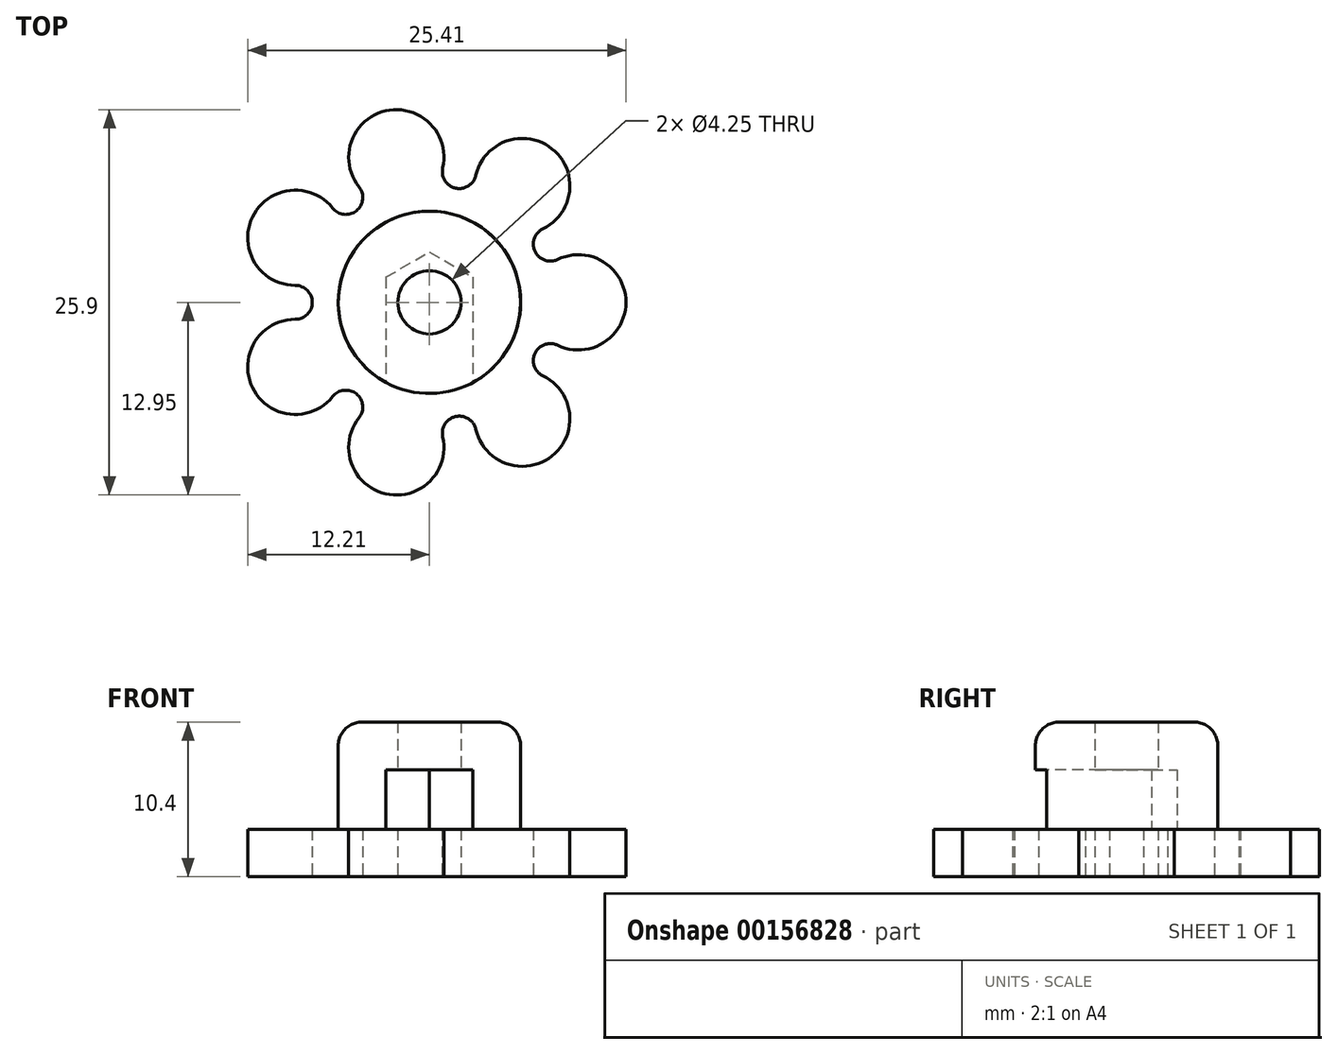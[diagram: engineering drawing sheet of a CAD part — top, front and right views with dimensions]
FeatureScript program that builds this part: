
annotation { "Feature Type Name" : "Feature", "Feature Type Description" : "" }
export const myFeature = defineFeature(function(context is Context, id is Id, definition is map)
    precondition{}
    {
        {
            var Q0;
            Q0=qCreatedBy(makeId("Top.planeOp"),FACE);
            var sketch = newSketch(context, id + "F0", { "sketchPlane" : qUnion([Q0])});
            skCircle(sketch, "E0", {"center": v(0, 0) * mm, "radius": 2.12 * mm});
            skArc(sketch, "E1", {"start": v(8.61, 2.88) * mm, "mid": v(13.2, 0) * mm, "end": v(8.61, -2.88) * mm});
            skArc(sketch, "E2.1.0", {"start": v(3.12, 8.53) * mm, "mid": v(8.23, 10.32) * mm, "end": v(7.62, 4.94) * mm});
            skArc(sketch, "E2.2.0", {"start": v(-4.73, 7.75) * mm, "mid": v(-2.94, 12.87) * mm, "end": v(0.9, 9.04) * mm});
            skArc(sketch, "E2.3.0", {"start": v(-9, 1.14) * mm, "mid": v(-11.9, 5.73) * mm, "end": v(-6.5, 6.33) * mm});
            skArc(sketch, "E2.4.0", {"start": v(-6.5, -6.33) * mm, "mid": v(-11.9, -5.73) * mm, "end": v(-9, -1.14) * mm});
            skArc(sketch, "E2.5.0", {"start": v(0.9, -9.04) * mm, "mid": v(-2.94, -12.87) * mm, "end": v(-4.73, -7.75) * mm});
            skArc(sketch, "E2.6.0", {"start": v(7.62, -4.94) * mm, "mid": v(8.23, -10.32) * mm, "end": v(3.12, -8.53) * mm});
            skLineSegment(sketch, "E3", {"start": v(7.62, -4.94) * mm, "end": v(8.61, -2.88) * mm, "construction": true});
            skArc(sketch, "E4", {"start": v(8.61, -2.88) * mm, "mid": v(7.1, -3.42) * mm, "end": v(7.62, -4.94) * mm});
            skArc(sketch, "E5.1.0", {"start": v(7.62, 4.94) * mm, "mid": v(7.1, 3.42) * mm, "end": v(8.61, 2.88) * mm});
            skArc(sketch, "E5.2.0", {"start": v(0.9, 9.04) * mm, "mid": v(1.75, 7.67) * mm, "end": v(3.12, 8.53) * mm});
            skArc(sketch, "E5.3.0", {"start": v(-6.5, 6.33) * mm, "mid": v(-4.9, 6.15) * mm, "end": v(-4.73, 7.75) * mm});
            skArc(sketch, "E5.4.0", {"start": v(-9, -1.14) * mm, "mid": v(-7.87, 0) * mm, "end": v(-9, 1.14) * mm});
            skArc(sketch, "E5.5.0", {"start": v(-4.73, -7.75) * mm, "mid": v(-4.9, -6.15) * mm, "end": v(-6.5, -6.33) * mm});
            skArc(sketch, "E5.6.0", {"start": v(3.12, -8.53) * mm, "mid": v(1.75, -7.67) * mm, "end": v(0.9, -9.04) * mm});
            skCircle(sketch, "E6.cCircle", {"center": v(0, 0) * mm, "radius": 2.93 * mm, "construction": true});
            skLineSegment(sketch, "E6.0", {"start": v(2.93, 1.69) * mm, "end": v(2.93, -1.69) * mm, "construction": true});
            skLineSegment(sketch, "E6.1", {"start": v(2.92, -1.69) * mm, "end": v(0, -3.38) * mm, "construction": true});
            skLineSegment(sketch, "E6.2", {"start": v(0, -3.38) * mm, "end": v(-2.92, -1.69) * mm, "construction": true});
            skLineSegment(sketch, "E6.3", {"start": v(-2.93, -1.69) * mm, "end": v(-2.93, 1.69) * mm, "construction": true});
            skLineSegment(sketch, "E6.4", {"start": v(-2.93, 1.69) * mm, "end": v(0, 3.38) * mm, "construction": true});
            skLineSegment(sketch, "E6.5", {"start": v(0, 3.38) * mm, "end": v(2.93, 1.69) * mm, "construction": true});
            skPoint(sketch, "E6.0.midPoint", {"position": v(2.93, 0) * mm});
            skSolve(sketch);
        }
        {
            var Q0;
            Q0=qSketchRegion(id+"F0",true);
            extrude(context, id + "F1", {"entities" : qUnion([Q0]), "depth" : 3.2 * mm});
        }
        {
            var Q0;
            Q0=makeQuery(id+"F1.opExtrude","CAP_FACE",FACE,{"disambiguationData":[OSD([sQuery(id+"F0.wireOp",EDGE,"E0"),sQuery(id+"F0.wireOp",EDGE,"E1"),sQuery(id+"F0.wireOp",EDGE,"E2.1.0"),sQuery(id+"F0.wireOp",EDGE,"E2.2.0"),sQuery(id+"F0.wireOp",EDGE,"E2.3.0"),sQuery(id+"F0.wireOp",EDGE,"E2.4.0"),sQuery(id+"F0.wireOp",EDGE,"E2.5.0"),sQuery(id+"F0.wireOp",EDGE,"E2.6.0"),sQuery(id+"F0.wireOp",EDGE,"E4"),sQuery(id+"F0.wireOp",EDGE,"E5.1.0"),sQuery(id+"F0.wireOp",EDGE,"E5.2.0"),sQuery(id+"F0.wireOp",EDGE,"E5.3.0"),sQuery(id+"F0.wireOp",EDGE,"E5.4.0"),sQuery(id+"F0.wireOp",EDGE,"E5.5.0"),sQuery(id+"F0.wireOp",EDGE,"E5.6.0")])],"isStart":false});
            var sketch = newSketch(context, id + "F2", { "sketchPlane" : qUnion([Q0])});
            skCircle(sketch, "E7.cCircle", {"center": v(0, 0) * mm, "radius": 2.92 * mm, "construction": true});
            skLineSegment(sketch, "E7.0", {"start": v(2.93, 1.69) * mm, "end": v(2.93, -1.69) * mm});
            skLineSegment(sketch, "E7.1", {"start": v(2.93, -1.69) * mm, "end": v(0, -3.38) * mm, "construction": true});
            skLineSegment(sketch, "E7.2", {"start": v(0, -3.38) * mm, "end": v(-2.92, -1.69) * mm, "construction": true});
            skLineSegment(sketch, "E7.3", {"start": v(-2.92, -1.69) * mm, "end": v(-2.93, 1.69) * mm});
            skLineSegment(sketch, "E7.4", {"start": v(-2.93, 1.69) * mm, "end": v(0, 3.38) * mm});
            skLineSegment(sketch, "E7.5", {"start": v(0, 3.38) * mm, "end": v(2.93, 1.69) * mm});
            skPoint(sketch, "E7.0.midPoint", {"position": v(2.92, 0) * mm});
            skArc(sketch, "E8", {"start": v(2.93, -5.38) * mm, "mid": v(0, 6.12) * mm, "end": v(-2.92, -5.38) * mm});
            skLineSegment(sketch, "E9", {"start": v(-2.92, -1.69) * mm, "end": v(-2.92, -5.38) * mm});
            skLineSegment(sketch, "E10", {"start": v(2.93, -1.69) * mm, "end": v(2.93, -5.38) * mm});
            skSolve(sketch);
        }
        {
            var Q0;
            Q0=qSketchRegion(id+"F2",true);
            var Q1;
            Q1=qConstructionFilter(qBodyType(qCreatedBy(id+"F2",EDGE),BodyType.WIRE),ConstructionObject.NO);
            extrude(context, id + "F3", {"entities" : qUnion([Q0]), "operationType" : NewBodyOperationType.ADD, "surfaceEntities" : qUnion([Q1]), "depth" : 4 * mm});
        }
        {
            var Q0;
            Q0=makeQuery(id+"F3.opExtrude","CAP_FACE",FACE,{"disambiguationData":[OSD([sQuery(id+"F2.wireOp",EDGE,"E7.0"),sQuery(id+"F2.wireOp",EDGE,"E7.3"),sQuery(id+"F2.wireOp",EDGE,"E7.4"),sQuery(id+"F2.wireOp",EDGE,"E7.5"),sQuery(id+"F2.wireOp",EDGE,"E8"),sQuery(id+"F2.wireOp",EDGE,"E9"),sQuery(id+"F2.wireOp",EDGE,"E10")])],"isStart":false});
            var sketch = newSketch(context, id + "F4", { "sketchPlane" : qUnion([Q0])});
            skCircle(sketch, "E11", {"center": v(0, 0) * mm, "radius": 2.12 * mm});
            skCircle(sketch, "E12", {"center": v(0, 0) * mm, "radius": 6.13 * mm});
            skSolve(sketch);
        }
        {
            var Q0;
            Q0=qSketchRegion(id+"F4",true);
            extrude(context, id + "F5", {"entities" : qUnion([Q0]), "operationType" : NewBodyOperationType.ADD, "depth" : 3.2 * mm});
        }
        {
            var Q0;
            Q0=makeQuery(id+"F3.opExtrude","CAP_EDGE",EDGE,{"disambiguationData":[OSD([sQuery(id+"F2.wireOp",EDGE,"E8")])],"isStart":true});
            var Q1;
            Q1=makeQuery(id+"F5.opExtrude","CAP_EDGE",EDGE,{"disambiguationData":[OSD([sQuery(id+"F4.wireOp",EDGE,"E12")])],"isStart":false});
            fillet(context, id + "F6", {"entities" : qUnion([Q0, Q1]), "radius" : 1.6 * mm, "tangentPropagation" : true, "allowEdgeOverflow" : false});
        }
    });
